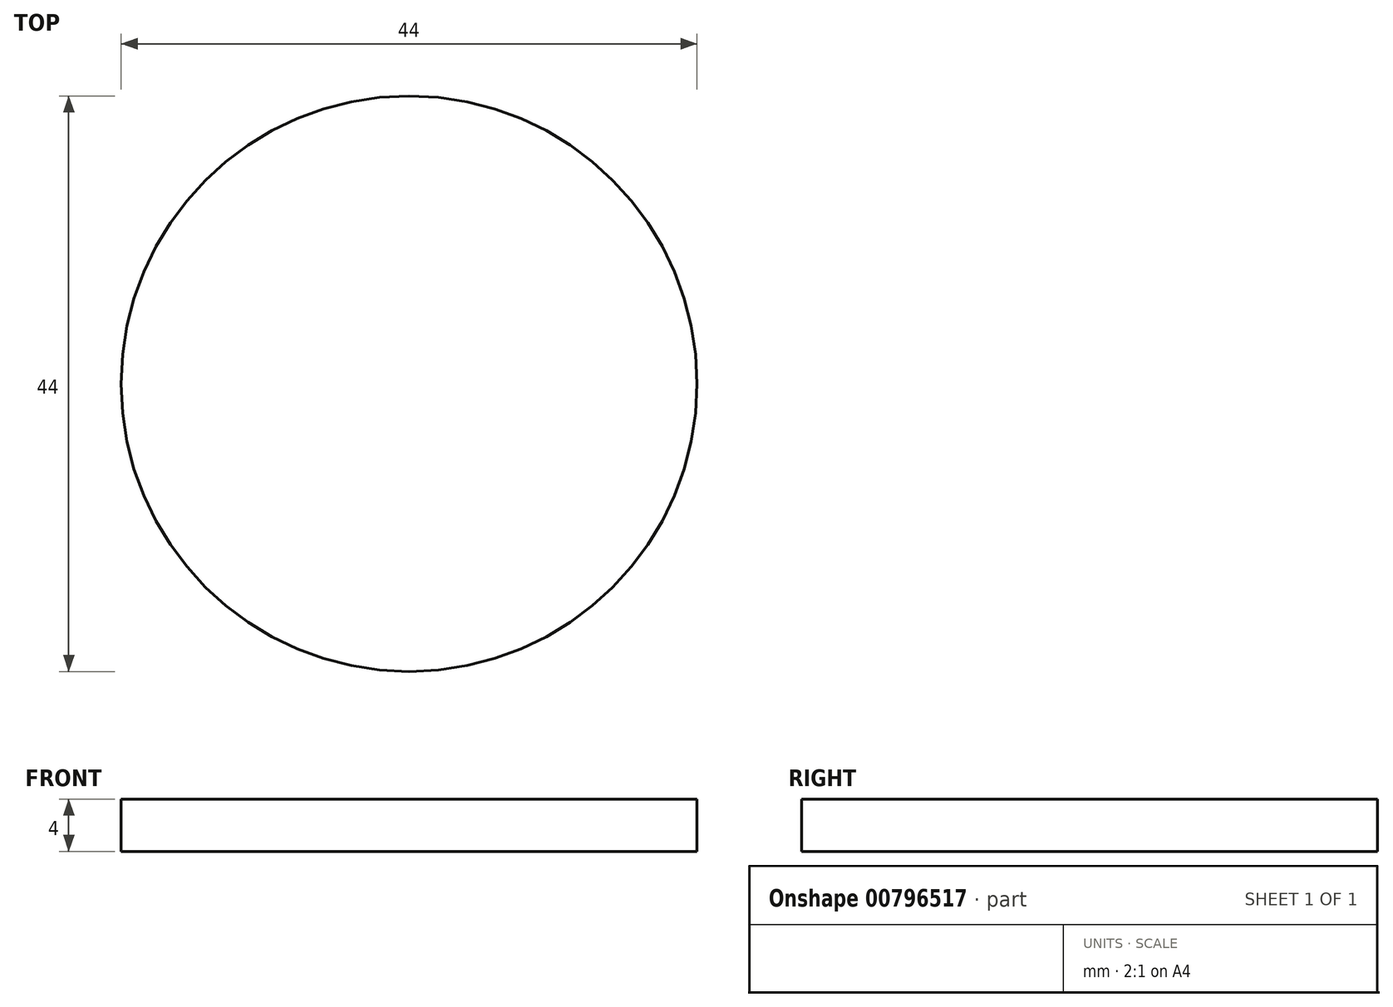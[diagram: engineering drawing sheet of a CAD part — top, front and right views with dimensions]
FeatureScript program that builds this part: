
annotation { "Feature Type Name" : "Feature", "Feature Type Description" : "" }
export const myFeature = defineFeature(function(context is Context, id is Id, definition is map)
    precondition{}
    {
        {
            var Q0;
            Q0=qCreatedBy(makeId("Top.planeOp"),FACE);
            var sketch = newSketch(context, id + "F0", { "sketchPlane" : qUnion([Q0])});
            skCircle(sketch, "E0", {"center": v(0, 0) * mm, "radius": 22 * mm});
            skCircle(sketch, "E1", {"center": v(0, 0) * mm, "radius": 20 * mm});
            skSolve(sketch);
        }
        {
            var Q0;
            Q0 = qSketchRegion(id + "F0", true);
            var Q1;
            Q1=makeQuery(id+"F0.imprint","IMPRINT",FACE,{"disambiguationData":[TD([[makeQuery(id+"F0.imprint","IMPRINT",EDGE,{"derivedFrom":sQuery(id+"F0.wireOp",EDGE,"E1")}),1.0]])]});
            extrude(context, id + "F1", {"entities" : qUnion([Q0, Q1]), "oppositeDirection" : true, "depth" : 4 * mm, "offsetDistance" : 25 * mm});
        }
    });
